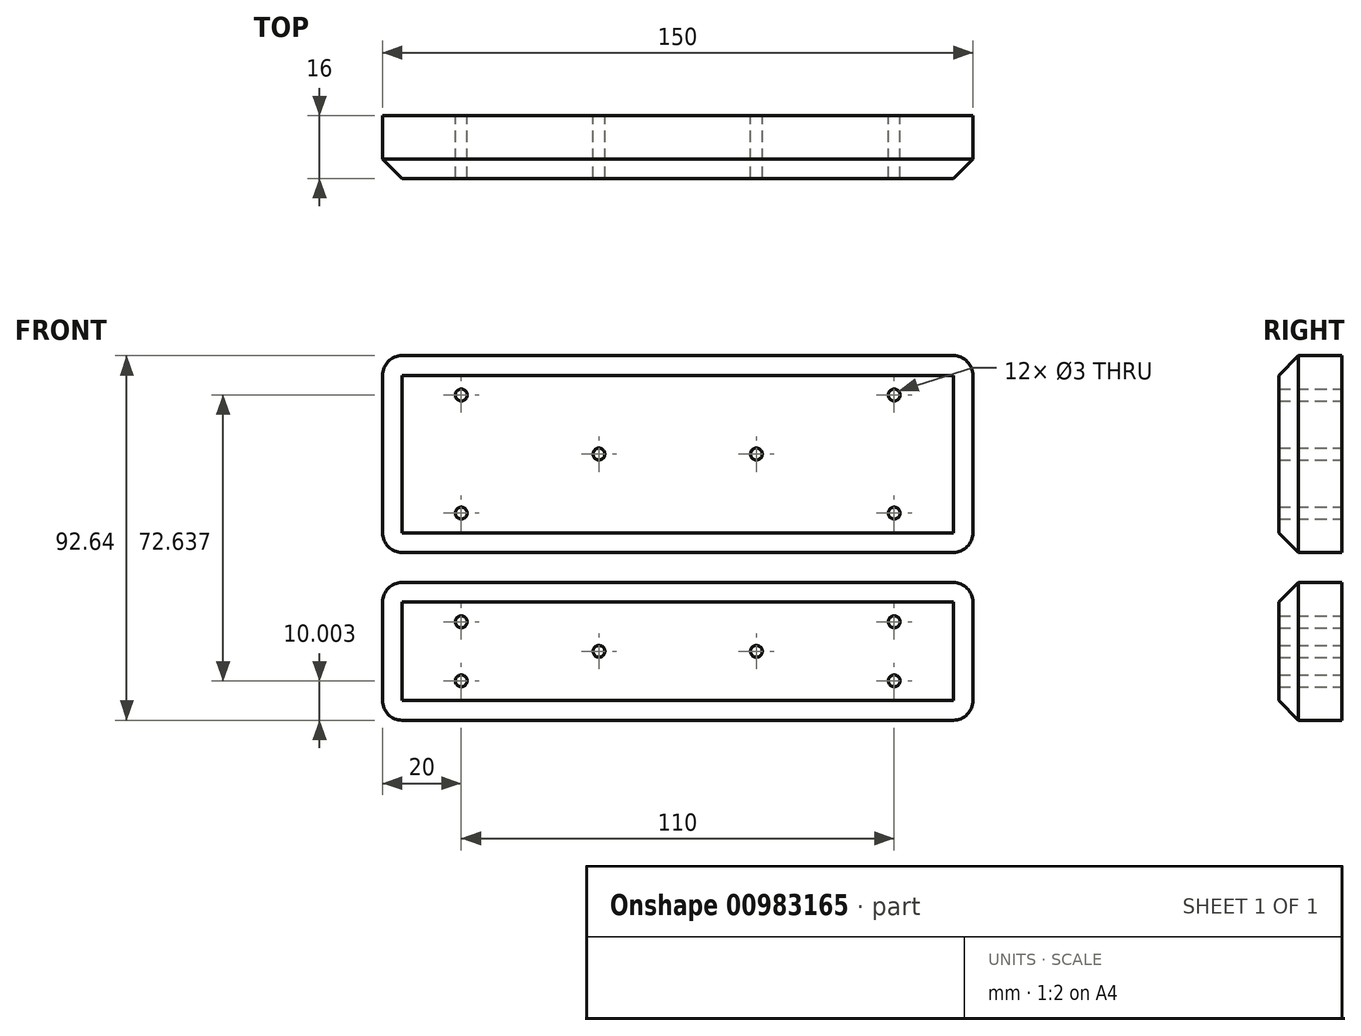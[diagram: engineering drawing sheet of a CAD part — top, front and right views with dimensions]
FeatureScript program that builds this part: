
annotation { "Feature Type Name" : "Feature", "Feature Type Description" : "" }
export const myFeature = defineFeature(function(context is Context, id is Id, definition is map)
    precondition{}
    {
        {
            var Q0;
            Q0=qCreatedBy(makeId("Front.planeOp"),FACE);
            var sketch = newSketch(context, id + "F0", { "sketchPlane" : qUnion([Q0])});
            skLineSegment(sketch, "E0.bottom", {"start": v(-70, 25) * mm, "end": v(70, 25) * mm});
            skLineSegment(sketch, "E0.top", {"start": v(-70, -25) * mm, "end": v(70, -25) * mm});
            skLineSegment(sketch, "E0.left", {"start": v(-75, 20) * mm, "end": v(-75, -20) * mm});
            skLineSegment(sketch, "E0.right", {"start": v(75, 20) * mm, "end": v(75, -20) * mm});
            skPoint(sketch, "E0.middle", {"position": v(0, 0) * mm});
            skLineSegment(sketch, "E1", {"start": v(0, 45.63) * mm, "end": v(0, -61.36) * mm, "construction": true});
            skLineSegment(sketch, "E2", {"start": v(116.41, 0) * mm, "end": v(-96.23, 0) * mm, "construction": true});
            skLineSegment(sketch, "E3", {"start": v(20, 36.9) * mm, "end": v(20, -62.5) * mm, "construction": true});
            skLineSegment(sketch, "E4", {"start": v(55, -46.84) * mm, "end": v(55, 54.37) * mm, "construction": true});
            skPoint(sketch, "E5", {"position": v(55, 15) * mm});
            skPoint(sketch, "E6", {"position": v(55, -15) * mm});
            skPoint(sketch, "E7", {"position": v(20, 0) * mm});
            skCircle(sketch, "E8", {"center": v(20, 0) * mm, "radius": 1.5 * mm});
            skCircle(sketch, "E9", {"center": v(55, 15) * mm, "radius": 1.5 * mm});
            skCircle(sketch, "E10", {"center": v(55, -15) * mm, "radius": 1.5 * mm});
            skPoint(sketch, "E11.visualSharp", {"position": v(75, 25) * mm});
            skArc(sketch, "E11.filletArc", {"start": v(75, 20) * mm, "mid": v(73.54, 23.54) * mm, "end": v(70, 25) * mm});
            skPoint(sketch, "E12.visualSharp", {"position": v(75, -25) * mm});
            skArc(sketch, "E12.filletArc", {"start": v(70, -25) * mm, "mid": v(73.54, -23.54) * mm, "end": v(75, -20) * mm});
            skArc(sketch, "E13.MirrorCS", {"start": v(-75, 20) * mm, "mid": v(-73.54, 23.54) * mm, "end": v(-70, 25) * mm});
            skArc(sketch, "E14.MirrorCS", {"start": v(-70, -25) * mm, "mid": v(-73.54, -23.54) * mm, "end": v(-75, -20) * mm});
            skPoint(sketch, "E15.orphan", {"position": v(-75, 25) * mm});
            skPoint(sketch, "E16.orphan", {"position": v(-75, -25) * mm});
            skCircle(sketch, "E17.MirrorC", {"center": v(-55, 15) * mm, "radius": 1.5 * mm});
            skCircle(sketch, "E18.MirrorC", {"center": v(-55, -15) * mm, "radius": 1.5 * mm});
            skCircle(sketch, "E19.MirrorC", {"center": v(-20, 0) * mm, "radius": 1.5 * mm});
            skLineSegment(sketch, "E20.left", {"start": v(-75, -37.64) * mm, "end": v(-75, -62.64) * mm});
            skLineSegment(sketch, "E20.right", {"start": v(75, -37.64) * mm, "end": v(75, -62.64) * mm});
            skPoint(sketch, "E20.middle", {"position": v(0, -50.14) * mm});
            skLineSegment(sketch, "E21", {"start": v(0, -4.5) * mm, "end": v(0, -111.5) * mm, "construction": true});
            skLineSegment(sketch, "E22", {"start": v(116.41, -50.14) * mm, "end": v(-96.23, -50.14) * mm, "construction": true});
            skLineSegment(sketch, "E23", {"start": v(20, -13.24) * mm, "end": v(20, -112.64) * mm, "construction": true});
            skLineSegment(sketch, "E24", {"start": v(55, -96.97) * mm, "end": v(55, 4.23) * mm, "construction": true});
            skPoint(sketch, "E25", {"position": v(55, -42.64) * mm});
            skPoint(sketch, "E26", {"position": v(55, -57.64) * mm});
            skPoint(sketch, "E27", {"position": v(20, -50.14) * mm});
            skCircle(sketch, "E28", {"center": v(20, -50.14) * mm, "radius": 1.5 * mm});
            skCircle(sketch, "E29", {"center": v(55, -42.64) * mm, "radius": 1.5 * mm});
            skCircle(sketch, "E30", {"center": v(55, -57.64) * mm, "radius": 1.5 * mm});
            skLineSegment(sketch, "E31", {"start": v(-70, -32.64) * mm, "end": v(70, -32.64) * mm});
            skPoint(sketch, "E32.visualSharp", {"position": v(-75, -32.64) * mm});
            skArc(sketch, "E32.filletArc", {"start": v(-70, -32.64) * mm, "mid": v(-73.54, -34.1) * mm, "end": v(-75, -37.64) * mm});
            skPoint(sketch, "E33.visualSharp", {"position": v(75, -32.64) * mm});
            skArc(sketch, "E33.filletArc", {"start": v(75, -37.64) * mm, "mid": v(73.54, -34.1) * mm, "end": v(70, -32.64) * mm});
            skLineSegment(sketch, "E34.MirrorCS", {"start": v(-70, -67.64) * mm, "end": v(70, -67.64) * mm});
            skArc(sketch, "E35.MirrorCS", {"start": v(-70, -67.64) * mm, "mid": v(-73.54, -66.17) * mm, "end": v(-75, -62.64) * mm});
            skArc(sketch, "E36.MirrorCS", {"start": v(75, -62.64) * mm, "mid": v(73.54, -66.17) * mm, "end": v(70, -67.64) * mm});
            skLineSegment(sketch, "E37", {"start": v(59.8, -57.64) * mm, "end": v(49.63, -57.64) * mm, "construction": true});
            skLineSegment(sketch, "E38", {"start": v(62.04, -42.64) * mm, "end": v(48.88, -42.64) * mm, "construction": true});
            skCircle(sketch, "E39.MirrorC", {"center": v(-55, -42.64) * mm, "radius": 1.5 * mm});
            skCircle(sketch, "E40.MirrorC", {"center": v(-55, -57.64) * mm, "radius": 1.5 * mm});
            skCircle(sketch, "E41.MirrorC", {"center": v(-20, -50.14) * mm, "radius": 1.5 * mm});
            skSolve(sketch);
        }
        {
            var Q0;
            Q0=makeQuery(id+"F0.imprint","IMPRINT",FACE,{"disambiguationData":[TD([[makeQuery(id+"F0.imprint","IMPRINT",EDGE,{"derivedFrom":sQuery(id+"F0.wireOp",EDGE,"E0.bottom")}),-1.0]])]});
            var Q1;
            Q1=makeQuery(id+"F0.imprint","IMPRINT",FACE,{"disambiguationData":[TD([[makeQuery(id+"F0.imprint","IMPRINT",EDGE,{"derivedFrom":sQuery(id+"F0.wireOp",EDGE,"E20.left")}),1.0]])]});
            extrude(context, id + "F1", {"entities" : qUnion([Q0, Q1]), "depth" : 16 * mm, "offsetDistance" : 25 * mm});
        }
        {
            var Q0;
            Q0=makeQuery(id+"F1.opExtrude","CAP_EDGE",EDGE,{"disambiguationData":[OSD([sQuery(id+"F0.wireOp",EDGE,"E0.bottom")])],"isStart":false});
            var Q1;
            Q1=makeQuery(id+"F1.opExtrude","CAP_EDGE",EDGE,{"disambiguationData":[OSD([sQuery(id+"F0.wireOp",EDGE,"E13.MirrorCS")])],"isStart":false});
            var Q2;
            Q2=makeQuery(id+"F1.opExtrude","CAP_EDGE",EDGE,{"disambiguationData":[OSD([sQuery(id+"F0.wireOp",EDGE,"E0.left")])],"isStart":false});
            var Q3;
            Q3=makeQuery(id+"F1.opExtrude","CAP_EDGE",EDGE,{"disambiguationData":[OSD([sQuery(id+"F0.wireOp",EDGE,"E14.MirrorCS")])],"isStart":false});
            var Q4;
            Q4=makeQuery(id+"F1.opExtrude","CAP_EDGE",EDGE,{"disambiguationData":[OSD([sQuery(id+"F0.wireOp",EDGE,"E0.top")])],"isStart":false});
            var Q5;
            Q5=makeQuery(id+"F1.opExtrude","CAP_EDGE",EDGE,{"disambiguationData":[OSD([sQuery(id+"F0.wireOp",EDGE,"E12.filletArc")])],"isStart":false});
            var Q6;
            Q6=makeQuery(id+"F1.opExtrude","CAP_EDGE",EDGE,{"disambiguationData":[OSD([sQuery(id+"F0.wireOp",EDGE,"E0.right")])],"isStart":false});
            var Q7;
            Q7=makeQuery(id+"F1.opExtrude","CAP_EDGE",EDGE,{"disambiguationData":[OSD([sQuery(id+"F0.wireOp",EDGE,"E11.filletArc")])],"isStart":false});
            var Q8;
            Q8=makeQuery(id+"F1.opExtrude","CAP_EDGE",EDGE,{"disambiguationData":[OSD([sQuery(id+"F0.wireOp",EDGE,"E31")])],"isStart":false});
            var Q9;
            Q9=makeQuery(id+"F1.opExtrude","CAP_EDGE",EDGE,{"disambiguationData":[OSD([sQuery(id+"F0.wireOp",EDGE,"E34.MirrorCS")])],"isStart":false});
            var Q10;
            Q10=makeQuery(id+"F1.opExtrude","CAP_EDGE",EDGE,{"disambiguationData":[OSD([sQuery(id+"F0.wireOp",EDGE,"E36.MirrorCS")])],"isStart":false});
            var Q11;
            Q11=makeQuery(id+"F1.opExtrude","CAP_EDGE",EDGE,{"disambiguationData":[OSD([sQuery(id+"F0.wireOp",EDGE,"E20.right")])],"isStart":false});
            var Q12;
            Q12=makeQuery(id+"F1.opExtrude","CAP_EDGE",EDGE,{"disambiguationData":[OSD([sQuery(id+"F0.wireOp",EDGE,"E33.filletArc")])],"isStart":false});
            var Q13;
            Q13=makeQuery(id+"F1.opExtrude","CAP_EDGE",EDGE,{"disambiguationData":[OSD([sQuery(id+"F0.wireOp",EDGE,"E32.filletArc")])],"isStart":false});
            var Q14;
            Q14=makeQuery(id+"F1.opExtrude","CAP_EDGE",EDGE,{"disambiguationData":[OSD([sQuery(id+"F0.wireOp",EDGE,"E20.left")])],"isStart":false});
            var Q15;
            Q15=makeQuery(id+"F1.opExtrude","CAP_EDGE",EDGE,{"disambiguationData":[OSD([sQuery(id+"F0.wireOp",EDGE,"E35.MirrorCS")])],"isStart":false});
            chamfer(context, id + "F2", {"entities" : qUnion([Q0, Q1, Q2, Q3, Q4, Q5, Q6, Q7, Q8, Q9, Q10, Q11, Q12, Q13, Q14, Q15]), "width" : 5 * mm, "tangentPropagation" : true});
        }
    });
